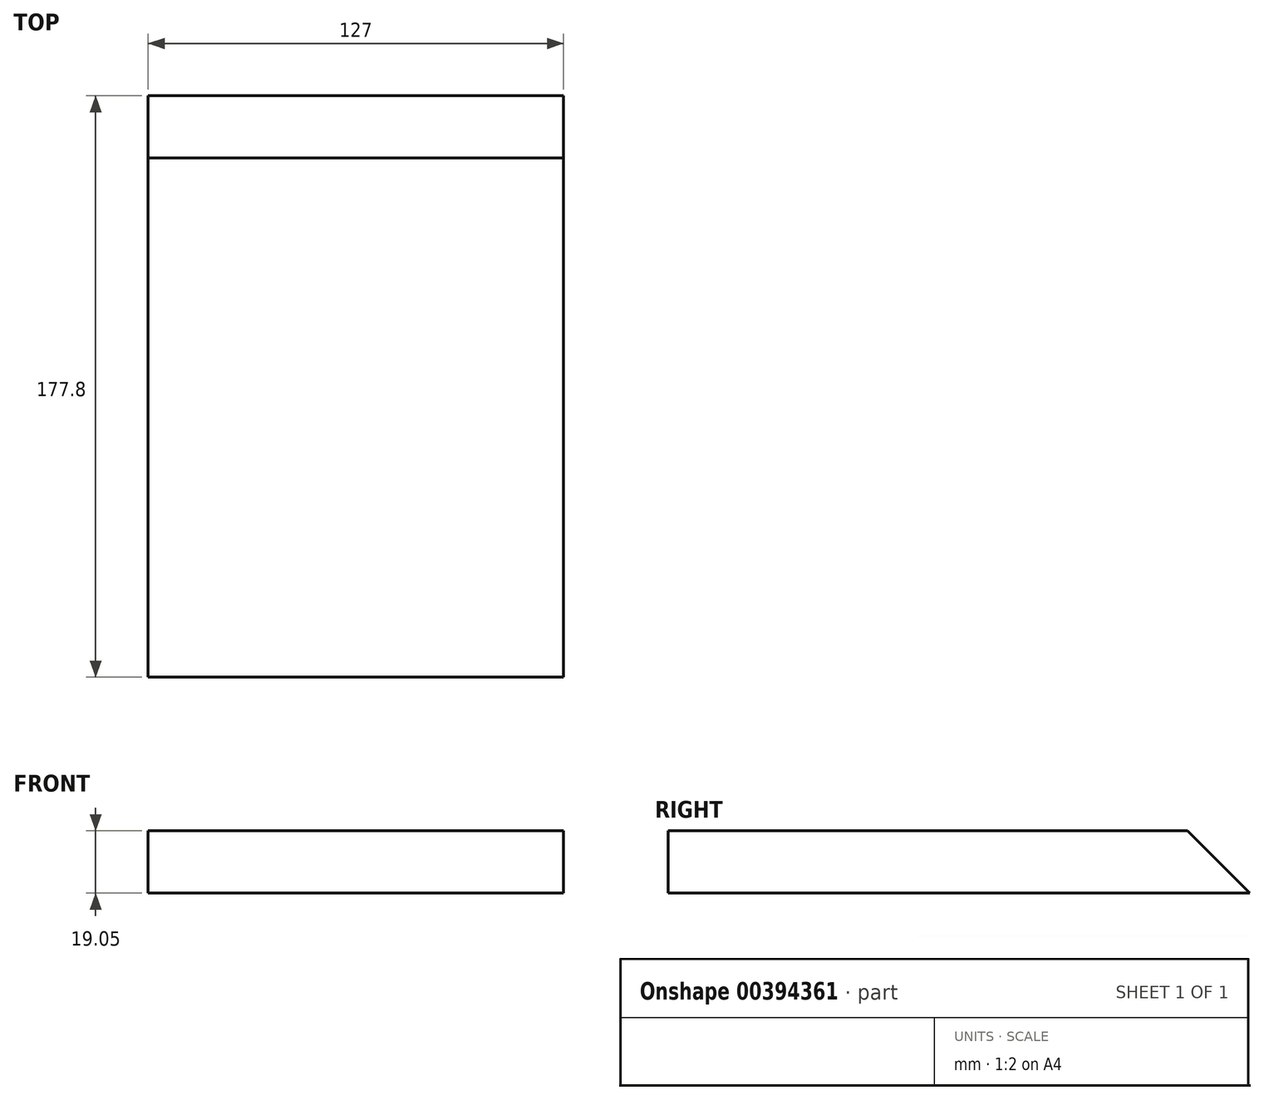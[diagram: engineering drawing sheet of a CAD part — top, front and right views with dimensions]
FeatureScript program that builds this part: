
annotation { "Feature Type Name" : "Feature", "Feature Type Description" : "" }
export const myFeature = defineFeature(function(context is Context, id is Id, definition is map)
    precondition{}
    {
        {
            var Q0;
            Q0=qCreatedBy(makeId("Top.planeOp"),FACE);
            var sketch = newSketch(context, id + "F0", { "sketchPlane" : qUnion([Q0])});
            skLineSegment(sketch, "E0", {"start": v(-69.95, 105.51) * mm, "end": v(57.05, 105.51) * mm});
            skLineSegment(sketch, "E1", {"start": v(57.05, 105.51) * mm, "end": v(57.05, -72.29) * mm});
            skLineSegment(sketch, "E2", {"start": v(57.05, -72.29) * mm, "end": v(-69.95, -72.29) * mm});
            skLineSegment(sketch, "E3", {"start": v(-69.95, -72.29) * mm, "end": v(-69.95, 105.51) * mm});
            skSolve(sketch);
        }
        {
            var Q0;
            Q0=makeQuery(id+"F0.imprint","IMPRINT",FACE,{"disambiguationData":[TD([[makeQuery(id+"F0.imprint","IMPRINT",EDGE,{"derivedFrom":sQuery(id+"F0.wireOp",EDGE,"E0")}),-1.0]])]});
            extrude(context, id + "F1", {"entities" : qUnion([Q0]), "depth" : 19.05 * mm});
        }
        {
            var Q0;
            Q0=makeQuery(id+"F1.opExtrude","SWEPT_FACE",FACE,{"disambiguationData":[OSD([sQuery(id+"F0.wireOp",EDGE,"E3")])]});
            var sketch = newSketch(context, id + "F2", { "sketchPlane" : qUnion([Q0])});
            skLineSegment(sketch, "E4", {"start": v(-105.51, 0) * mm, "end": v(-86.46, 19.05) * mm});
            skSolve(sketch);
        }
        {
            var Q0;
            {var subQ0=sQuery(id+"F2.wireOp",EDGE,"E4");Q0=makeQuery(id+"F2.imprint","IMPRINT",FACE,{"disambiguationData":[TD([[makeQuery(id+"F2.imprint","IMPRINT",EDGE,{"derivedFrom":subQ0}),1.0]])]});}
            extrude(context, id + "F3", {"entities" : qUnion([Q0]), "operationType" : NewBodyOperationType.REMOVE, "oppositeDirection" : true, "depth" : 127 * mm});
        }
    });
